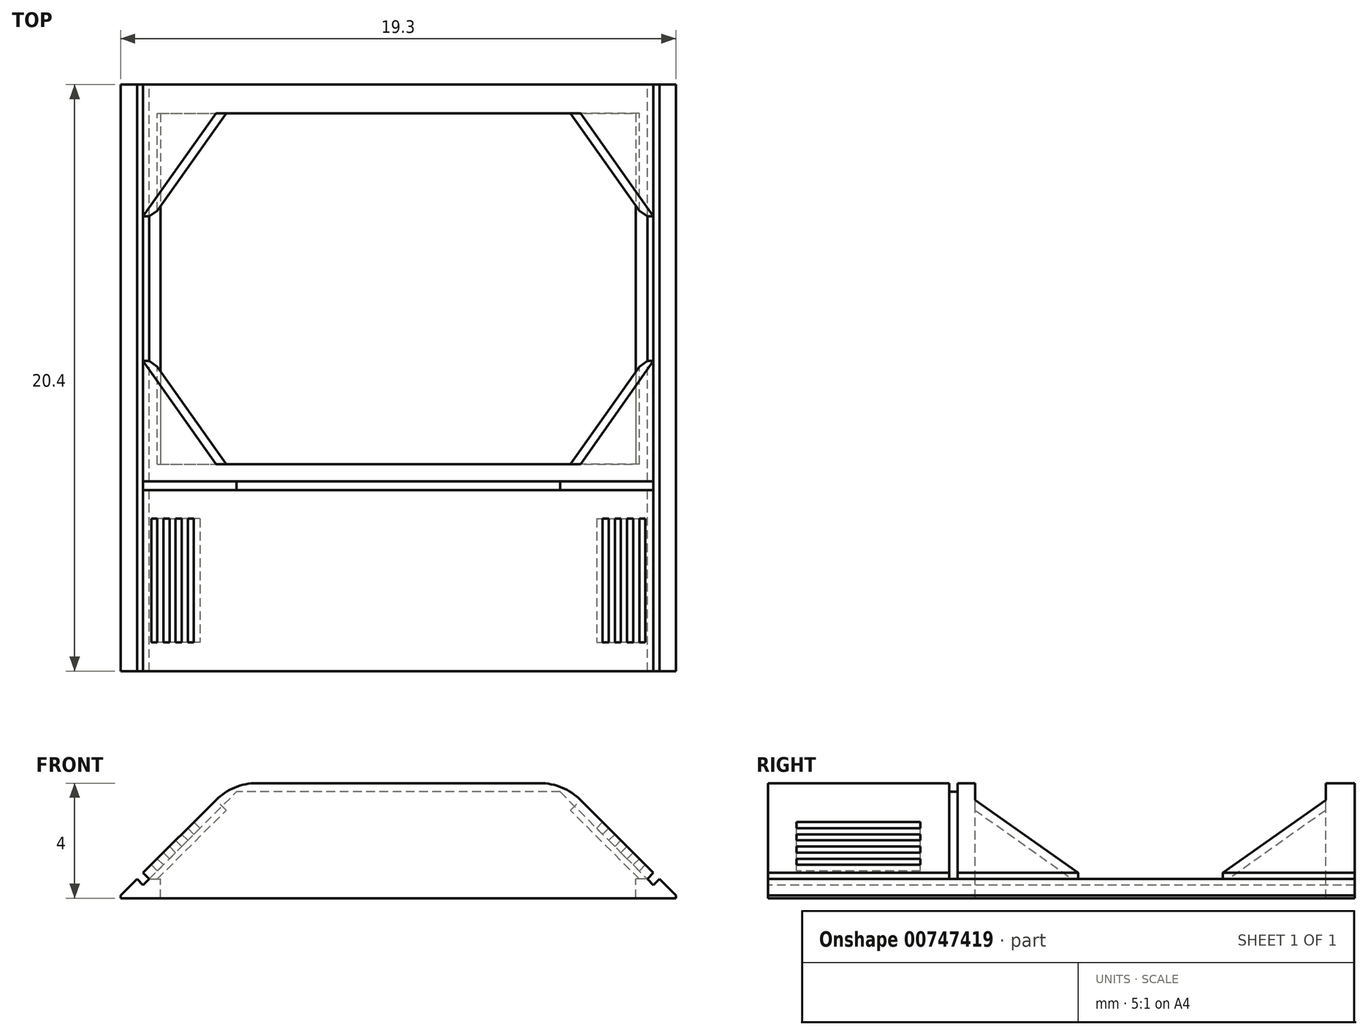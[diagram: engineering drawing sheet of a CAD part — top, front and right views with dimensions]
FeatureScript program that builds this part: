
annotation { "Feature Type Name" : "Feature", "Feature Type Description" : "" }
export const myFeature = defineFeature(function(context is Context, id is Id, definition is map)
    precondition{}
    {
        {
            var Q0;
            Q0=qCreatedBy(makeId("Front.planeOp"),FACE);
            var sketch = newSketch(context, id + "F0", { "sketchPlane" : qUnion([Q0])});
            skLineSegment(sketch, "E0", {"start": v(0, 0) * mm, "end": v(0, 3.9) * mm});
            skLineSegment(sketch, "E1", {"start": v(0, 3.9) * mm, "end": v(-5.75, 3.9) * mm});
            skLineSegment(sketch, "E2", {"start": v(-5.75, 3.9) * mm, "end": v(-9.65, 0) * mm});
            skLineSegment(sketch, "E3", {"start": v(-9.65, 0) * mm, "end": v(0, 0) * mm});
            skSolve(sketch);
        }
        {
            var Q0;
            Q0 = qSketchRegion(id + "F0", true);
            extrude(context, id + "F1", {"entities" : qUnion([Q0]), "depth" : 20.4 * mm, "offsetDistance" : 25 * mm});
        }
        {
            var Q0;
            Q0=makeQuery(id+"F1.opExtrude","SWEPT_FACE",FACE,{"disambiguationData":[OSD([sQuery(id+"F0.wireOp",EDGE,"E2")])]});
            var sketch = newSketch(context, id + "F2", { "sketchPlane" : qUnion([Q0])});
            skLineSegment(sketch, "E4", {"start": v(0, -5.72) * mm, "end": v(0, -6.02) * mm});
            skLineSegment(sketch, "E5", {"start": v(0, -6.02) * mm, "end": v(20.4, -6.02) * mm});
            skLineSegment(sketch, "E6", {"start": v(20.4, -5.72) * mm, "end": v(14.1, -5.72) * mm});
            skLineSegment(sketch, "E7", {"start": v(14.1, -5.72) * mm, "end": v(14.1, 0.2) * mm});
            skLineSegment(sketch, "E8", {"start": v(14.1, 0.2) * mm, "end": v(13.8, 0.2) * mm});
            skLineSegment(sketch, "E9", {"start": v(13.8, 0.2) * mm, "end": v(13.8, -5.72) * mm});
            skLineSegment(sketch, "E10", {"start": v(13.8, -5.72) * mm, "end": v(0, -5.72) * mm});
            skLineSegment(sketch, "E11", {"start": v(20.4, -5.72) * mm, "end": v(20.4, -6.02) * mm});
            skSolve(sketch);
        }
        {
            var Q0;
            Q0 = qSketchRegion(id + "F2", true);
            extrude(context, id + "F3", {"entities" : qUnion([Q0]), "operationType" : NewBodyOperationType.REMOVE, "oppositeDirection" : true, "depth" : 0.3 * mm, "offsetDistance" : 25 * mm});
        }
        {
            var Q0;
            Q0=makeQuery(id+"F1.opExtrude","SWEPT_FACE",FACE,{"disambiguationData":[OSD([sQuery(id+"F0.wireOp",EDGE,"E0")])]});
            var sketch = newSketch(context, id + "F4", { "sketchPlane" : qUnion([Q0])});
            skLineSegment(sketch, "E12", {"start": v(-13.2, 3.9) * mm, "end": v(-13.2, 0.57) * mm});
            skLineSegment(sketch, "E13", {"start": v(-13.2, 0.57) * mm, "end": v(-1, 0.57) * mm});
            skLineSegment(sketch, "E14", {"start": v(-1, 0.57) * mm, "end": v(-1, 3.9) * mm});
            skLineSegment(sketch, "E15", {"start": v(-1, 3.9) * mm, "end": v(-13.2, 3.9) * mm});
            skSolve(sketch);
        }
        {
            var Q0;
            Q0 = qSketchRegion(id + "F4", true);
            extrude(context, id + "F5", {"entities" : qUnion([Q0]), "operationType" : NewBodyOperationType.REMOVE, "endBound" : BoundingType.UP_TO_NEXT, "oppositeDirection" : true, "depth" : 25 * mm, "offsetDistance" : 25 * mm});
        }
        {
            var Q0;
            Q0=makeQuery(id+"F5.boolean.opBoolean","COPY",FACE,{"derivedFrom":makeQuery(id+"F5.opExtrude","SWEPT_FACE",FACE,{"disambiguationData":[OSD([sQuery(id+"F4.wireOp",EDGE,"E13")])]})});
            var sketch = newSketch(context, id + "F6", { "sketchPlane" : qUnion([Q0])});
            skLineSegment(sketch, "E16.bottom", {"start": v(0, -1) * mm, "end": v(-8.26, -1) * mm});
            skLineSegment(sketch, "E16.top", {"start": v(0, -13.2) * mm, "end": v(-8.26, -13.2) * mm});
            skLineSegment(sketch, "E16.left", {"start": v(0, -1) * mm, "end": v(0, -13.2) * mm});
            skLineSegment(sketch, "E16.right", {"start": v(-8.26, -1) * mm, "end": v(-8.26, -13.2) * mm});
            skSolve(sketch);
        }
        {
            var Q0;
            Q0 = qSketchRegion(id + "F6", true);
            extrude(context, id + "F7", {"entities" : qUnion([Q0]), "operationType" : NewBodyOperationType.REMOVE, "oppositeDirection" : true, "depth" : 25 * mm, "offsetDistance" : 25 * mm});
        }
        {
            var Q0;
            {var subQ0=sQuery(id+"F0.wireOp",EDGE,"E2");Q0=makeQuery(id+"F3.boolean.opBoolean","SPLIT",FACE,{"disambiguationData":[TD([makeQuery(id+"F3.opExtrude","SWEPT_FACE",FACE,{"disambiguationData":[OSD([sQuery(id+"F2.wireOp",EDGE,"E6")])]})])],"derivedFrom":makeQuery(id+"F1.opExtrude","SWEPT_FACE",FACE,{"disambiguationData":[OSD([subQ0])]})});}
            var sketch = newSketch(context, id + "F8", { "sketchPlane" : qUnion([Q0])});
            skLineSegment(sketch, "E17.bottom", {"start": v(15.1, -3.22) * mm, "end": v(19.4, -3.22) * mm});
            skLineSegment(sketch, "E17.top", {"start": v(15.1, -3.52) * mm, "end": v(19.4, -3.52) * mm});
            skLineSegment(sketch, "E17.left", {"start": v(15.1, -3.22) * mm, "end": v(15.1, -3.52) * mm});
            skLineSegment(sketch, "E17.right", {"start": v(19.4, -3.22) * mm, "end": v(19.4, -3.52) * mm});
            skLineSegment(sketch, "E18.bottom", {"start": v(15.1, -3.82) * mm, "end": v(19.4, -3.82) * mm});
            skLineSegment(sketch, "E18.top", {"start": v(15.1, -4.12) * mm, "end": v(19.4, -4.12) * mm});
            skLineSegment(sketch, "E18.left", {"start": v(15.1, -3.82) * mm, "end": v(15.1, -4.12) * mm});
            skLineSegment(sketch, "E18.right", {"start": v(19.4, -3.82) * mm, "end": v(19.4, -4.12) * mm});
            skLineSegment(sketch, "E19.bottom", {"start": v(15.1, -5.02) * mm, "end": v(19.4, -5.02) * mm});
            skLineSegment(sketch, "E19.top", {"start": v(15.1, -5.32) * mm, "end": v(19.4, -5.32) * mm});
            skLineSegment(sketch, "E19.left", {"start": v(15.1, -5.02) * mm, "end": v(15.1, -5.32) * mm});
            skLineSegment(sketch, "E19.right", {"start": v(19.4, -5.02) * mm, "end": v(19.4, -5.32) * mm});
            skLineSegment(sketch, "E20", {"start": v(19.4, -3.82) * mm, "end": v(19.4, -3.52) * mm, "construction": true});
            skLineSegment(sketch, "E21.bottom", {"start": v(15.1, -4.72) * mm, "end": v(19.4, -4.72) * mm});
            skLineSegment(sketch, "E21.top", {"start": v(15.1, -4.42) * mm, "end": v(19.4, -4.42) * mm});
            skLineSegment(sketch, "E21.left", {"start": v(15.1, -4.72) * mm, "end": v(15.1, -4.42) * mm});
            skLineSegment(sketch, "E21.right", {"start": v(19.4, -4.72) * mm, "end": v(19.4, -4.42) * mm});
            skLineSegment(sketch, "E22", {"start": v(19.4, -5.02) * mm, "end": v(19.4, -4.72) * mm, "construction": true});
            skLineSegment(sketch, "E23", {"start": v(19.4, -4.42) * mm, "end": v(19.4, -4.12) * mm, "construction": true});
            skSolve(sketch);
        }
        {
            var Q0;
            Q0 = qSketchRegion(id + "F8", true);
            extrude(context, id + "F9", {"entities" : qUnion([Q0]), "operationType" : NewBodyOperationType.REMOVE, "oppositeDirection" : true, "depth" : 0.3 * mm, "offsetDistance" : 25 * mm});
        }
        {
            var Q0;
            {var subQ0=sQuery(id+"F0.wireOp",EDGE,"E2");var subQ1=sQuery(id+"F0.wireOp",EDGE,"E1");Q0=makeQuery(id+"F3.boolean.opBoolean","SPLIT",EDGE,{"disambiguationData":[TD([makeQuery(id+"F3.opExtrude","SWEPT_FACE",FACE,{"disambiguationData":[OSD([sQuery(id+"F2.wireOp",EDGE,"f21vu9gR-xKNE-jHTs-my54-qgl62lx18LQn")])]})])],"derivedFrom":makeQuery(id+"F1.opExtrude","SWEPT_EDGE",EDGE,{"disambiguationData":[OSD([subQ1,subQ0])]})});}
            var Q1;
            Q1=makeQuery(id+"F9.boolean.opBoolean","INTERSECT",EDGE,{"derivedFrom":[makeQuery(id+"F3.boolean.opBoolean","COPY",FACE,{"derivedFrom":makeQuery(id+"F3.opExtrude","CAP_FACE",FACE,{"disambiguationData":[OSD([sQuery(id+"F2.wireOp",EDGE,"E4"),sQuery(id+"F2.wireOp",EDGE,"E5"),sQuery(id+"F2.wireOp",EDGE,"W1S3Mdm3-XKtb-n79g-vNsw-S0DXEWbo00DY"),sQuery(id+"F2.wireOp",EDGE,"qYD3X6LT-LOBn-4FV6-n4hA-iwyxqi3YV5cj"),sQuery(id+"F2.wireOp",EDGE,"E6"),sQuery(id+"F2.wireOp",EDGE,"E7"),sQuery(id+"F2.wireOp",EDGE,"E8"),sQuery(id+"F2.wireOp",EDGE,"E9"),sQuery(id+"F2.wireOp",EDGE,"E10"),sQuery(id+"F2.wireOp",EDGE,"NPIpTUiE-nrGw-dl87-8o0Y-yswYt9O5n7NW"),sQuery(id+"F2.wireOp",EDGE,"A6FpXCl3-eOSp-HMbo-aC3y-wrRHpwpuDLvK"),sQuery(id+"F2.wireOp",EDGE,"f21vu9gR-xKNE-jHTs-my54-qgl62lx18LQn"),sQuery(id+"F2.wireOp",EDGE,"PXoNwWFW-rPbD-wsng-xjVY-AKnaFY8J5v1U"),sQuery(id+"F2.wireOp",EDGE,"QdudRzUA-Mg1N-fK48-y1j2-ZxyqQCj9d9Z8")])],"isStart":false})}),makeQuery(id+"F9.opExtrude","CAP_FACE",FACE,{"disambiguationData":[OSD([sQuery(id+"F8.wireOp",EDGE,"rv0lEkuu-8LjM-F8fy-3w45-rrlrnGDjvpog.bottom"),sQuery(id+"F8.wireOp",EDGE,"rv0lEkuu-8LjM-F8fy-3w45-rrlrnGDjvpog.top"),sQuery(id+"F8.wireOp",EDGE,"rv0lEkuu-8LjM-F8fy-3w45-rrlrnGDjvpog.left"),sQuery(id+"F8.wireOp",EDGE,"rv0lEkuu-8LjM-F8fy-3w45-rrlrnGDjvpog.right")])],"isStart":false})]});
            var Q2;
            {var subQ0=sQuery(id+"F0.wireOp",EDGE,"E1");var subQ2=sQuery(id+"F0.wireOp",EDGE,"E2");var subQ4=makeQuery(id+"F3.opExtrude","SWEPT_FACE",FACE,{"disambiguationData":[OSD([sQuery(id+"F2.wireOp",EDGE,"NPIpTUiE-nrGw-dl87-8o0Y-yswYt9O5n7NW")])]});Q2=makeQuery(id+"F5.boolean.opBoolean","SPLIT",EDGE,{"disambiguationData":[TD([makeQuery(id+"F3.boolean.opBoolean","COPY",FACE,{"derivedFrom":subQ4})])],"derivedFrom":makeQuery(id+"F3.boolean.opBoolean","SPLIT",EDGE,{"disambiguationData":[TD([makeQuery(id+"F3.opExtrude","SWEPT_FACE",FACE,{"disambiguationData":[OSD([sQuery(id+"F2.wireOp",EDGE,"E9")])]})])],"derivedFrom":makeQuery(id+"F1.opExtrude","SWEPT_EDGE",EDGE,{"disambiguationData":[OSD([subQ0,subQ2])]})})});}
            var Q3;
            {var subQ0=sQuery(id+"F0.wireOp",EDGE,"E1");var subQ2=sQuery(id+"F0.wireOp",EDGE,"E2");var subQ4=makeQuery(id+"F3.opExtrude","SWEPT_FACE",FACE,{"disambiguationData":[OSD([sQuery(id+"F2.wireOp",EDGE,"E9")])]});Q3=makeQuery(id+"F5.boolean.opBoolean","SPLIT",EDGE,{"disambiguationData":[TD([makeQuery(id+"F3.boolean.opBoolean","COPY",FACE,{"derivedFrom":subQ4})])],"derivedFrom":makeQuery(id+"F3.boolean.opBoolean","SPLIT",EDGE,{"disambiguationData":[TD([subQ4])],"derivedFrom":makeQuery(id+"F1.opExtrude","SWEPT_EDGE",EDGE,{"disambiguationData":[OSD([subQ0,subQ2])]})})});}
            var Q4;
            Q4=makeQuery(id+"F9.boolean.opBoolean","INTERSECT",EDGE,{"derivedFrom":[makeQuery(id+"F3.boolean.opBoolean","COPY",FACE,{"derivedFrom":makeQuery(id+"F3.opExtrude","CAP_FACE",FACE,{"disambiguationData":[OSD([sQuery(id+"F2.wireOp",EDGE,"E4"),sQuery(id+"F2.wireOp",EDGE,"E5"),sQuery(id+"F2.wireOp",EDGE,"W1S3Mdm3-XKtb-n79g-vNsw-S0DXEWbo00DY"),sQuery(id+"F2.wireOp",EDGE,"qYD3X6LT-LOBn-4FV6-n4hA-iwyxqi3YV5cj"),sQuery(id+"F2.wireOp",EDGE,"E6"),sQuery(id+"F2.wireOp",EDGE,"E7"),sQuery(id+"F2.wireOp",EDGE,"E8"),sQuery(id+"F2.wireOp",EDGE,"E9"),sQuery(id+"F2.wireOp",EDGE,"E10"),sQuery(id+"F2.wireOp",EDGE,"NPIpTUiE-nrGw-dl87-8o0Y-yswYt9O5n7NW"),sQuery(id+"F2.wireOp",EDGE,"A6FpXCl3-eOSp-HMbo-aC3y-wrRHpwpuDLvK"),sQuery(id+"F2.wireOp",EDGE,"f21vu9gR-xKNE-jHTs-my54-qgl62lx18LQn"),sQuery(id+"F2.wireOp",EDGE,"PXoNwWFW-rPbD-wsng-xjVY-AKnaFY8J5v1U"),sQuery(id+"F2.wireOp",EDGE,"QdudRzUA-Mg1N-fK48-y1j2-ZxyqQCj9d9Z8")])],"isStart":false})}),makeQuery(id+"F9.opExtrude","CAP_FACE",FACE,{"disambiguationData":[OSD([sQuery(id+"F8.wireOp",EDGE,"9kW2MHKQ-ooD5-zoGo-1hlY-vFjgnSLi35nN.bottom"),sQuery(id+"F8.wireOp",EDGE,"9kW2MHKQ-ooD5-zoGo-1hlY-vFjgnSLi35nN.top"),sQuery(id+"F8.wireOp",EDGE,"9kW2MHKQ-ooD5-zoGo-1hlY-vFjgnSLi35nN.left"),sQuery(id+"F8.wireOp",EDGE,"9kW2MHKQ-ooD5-zoGo-1hlY-vFjgnSLi35nN.right")])],"isStart":false})]});
            var Q5;
            {var subQ0=sQuery(id+"F0.wireOp",EDGE,"E1");var subQ1=sQuery(id+"F0.wireOp",EDGE,"E2");Q5=makeQuery(id+"F3.boolean.opBoolean","SPLIT",EDGE,{"disambiguationData":[TD([makeQuery(id+"F3.opExtrude","SWEPT_FACE",FACE,{"disambiguationData":[OSD([sQuery(id+"F2.wireOp",EDGE,"qYD3X6LT-LOBn-4FV6-n4hA-iwyxqi3YV5cj")])]})])],"derivedFrom":makeQuery(id+"F1.opExtrude","SWEPT_EDGE",EDGE,{"disambiguationData":[OSD([subQ0,subQ1])]})});}
            var Q6;
            Q6=makeQuery(id+"F9.boolean.opBoolean","INTERSECT",EDGE,{"derivedFrom":[makeQuery(id+"F3.boolean.opBoolean","COPY",FACE,{"derivedFrom":makeQuery(id+"F3.opExtrude","CAP_FACE",FACE,{"disambiguationData":[OSD([sQuery(id+"F2.wireOp",EDGE,"E4"),sQuery(id+"F2.wireOp",EDGE,"E5"),sQuery(id+"F2.wireOp",EDGE,"W1S3Mdm3-XKtb-n79g-vNsw-S0DXEWbo00DY"),sQuery(id+"F2.wireOp",EDGE,"qYD3X6LT-LOBn-4FV6-n4hA-iwyxqi3YV5cj"),sQuery(id+"F2.wireOp",EDGE,"E6"),sQuery(id+"F2.wireOp",EDGE,"E7"),sQuery(id+"F2.wireOp",EDGE,"E8"),sQuery(id+"F2.wireOp",EDGE,"E9"),sQuery(id+"F2.wireOp",EDGE,"E10"),sQuery(id+"F2.wireOp",EDGE,"NPIpTUiE-nrGw-dl87-8o0Y-yswYt9O5n7NW"),sQuery(id+"F2.wireOp",EDGE,"A6FpXCl3-eOSp-HMbo-aC3y-wrRHpwpuDLvK"),sQuery(id+"F2.wireOp",EDGE,"f21vu9gR-xKNE-jHTs-my54-qgl62lx18LQn"),sQuery(id+"F2.wireOp",EDGE,"PXoNwWFW-rPbD-wsng-xjVY-AKnaFY8J5v1U"),sQuery(id+"F2.wireOp",EDGE,"QdudRzUA-Mg1N-fK48-y1j2-ZxyqQCj9d9Z8")])],"isStart":false})}),makeQuery(id+"F9.opExtrude","CAP_FACE",FACE,{"disambiguationData":[OSD([sQuery(id+"F8.wireOp",EDGE,"ZSyIJnYn-PckX-nyar-pei3-2CxvSKr0QWU7.bottom"),sQuery(id+"F8.wireOp",EDGE,"ZSyIJnYn-PckX-nyar-pei3-2CxvSKr0QWU7.top"),sQuery(id+"F8.wireOp",EDGE,"ZSyIJnYn-PckX-nyar-pei3-2CxvSKr0QWU7.left"),sQuery(id+"F8.wireOp",EDGE,"ZSyIJnYn-PckX-nyar-pei3-2CxvSKr0QWU7.right")])],"isStart":false})]});
            var Q7;
            {var subQ0=sQuery(id+"F0.wireOp",EDGE,"E2");var subQ1=sQuery(id+"F0.wireOp",EDGE,"E1");Q7=makeQuery(id+"F3.boolean.opBoolean","SPLIT",EDGE,{"disambiguationData":[TD([makeQuery(id+"F3.opExtrude","SWEPT_FACE",FACE,{"disambiguationData":[OSD([sQuery(id+"F2.wireOp",EDGE,"QdudRzUA-Mg1N-fK48-y1j2-ZxyqQCj9d9Z8")])]})])],"derivedFrom":makeQuery(id+"F1.opExtrude","SWEPT_EDGE",EDGE,{"disambiguationData":[OSD([subQ1,subQ0])]})});}
            var Q8;
            {var subQ0=sQuery(id+"F0.wireOp",EDGE,"E2");var subQ1=sQuery(id+"F0.wireOp",EDGE,"E1");Q8=makeQuery(id+"F5.boolean.opBoolean","SPLIT",EDGE,{"disambiguationData":[TD([makeQuery(id+"F5.opExtrude","SWEPT_FACE",FACE,{"disambiguationData":[OSD([sQuery(id+"F4.wireOp",EDGE,"E14")])]})])],"derivedFrom":makeQuery(id+"F3.boolean.opBoolean","SPLIT",EDGE,{"disambiguationData":[TD([makeQuery(id+"F3.opExtrude","SWEPT_FACE",FACE,{"disambiguationData":[OSD([sQuery(id+"F2.wireOp",EDGE,"E9")])]})])],"derivedFrom":makeQuery(id+"F1.opExtrude","SWEPT_EDGE",EDGE,{"disambiguationData":[OSD([subQ1,subQ0])]})})});}
            fillet(context, id + "F10", {"entities" : qUnion([Q0, Q1, Q2, Q3, Q4, Q5, Q6, Q7, Q8]), "radius" : 2 * mm, "tangentPropagation" : true, "allowEdgeOverflow" : false});
        }
        {
            var Q0;
            {var subQ1=makeQuery(id+"F3.opExtrude","SWEPT_FACE",FACE,{"disambiguationData":[OSD([sQuery(id+"F2.wireOp",EDGE,"E9")])]});Q0=makeQuery(id+"F5.boolean.opBoolean","SPLIT",FACE,{"disambiguationData":[TD([makeQuery(id+"F3.boolean.opBoolean","COPY",FACE,{"derivedFrom":subQ1})])],"derivedFrom":makeQuery(id+"F3.boolean.opBoolean","SPLIT",FACE,{"disambiguationData":[TD([subQ1])],"derivedFrom":makeQuery(id+"F1.opExtrude","SWEPT_FACE",FACE,{"disambiguationData":[OSD([sQuery(id+"F0.wireOp",EDGE,"E2")])]})})});}
            var sketch = newSketch(context, id + "F11", { "sketchPlane" : qUnion([Q0])});
            skLineSegment(sketch, "E24", {"start": v(13.2, -2.14) * mm, "end": v(9.61, -5.72) * mm});
            skLineSegment(sketch, "E25", {"start": v(9.61, -5.72) * mm, "end": v(13.2, -5.72) * mm});
            skLineSegment(sketch, "E26", {"start": v(1, -5.72) * mm, "end": v(1, -2.14) * mm});
            skLineSegment(sketch, "E27", {"start": v(1, -2.14) * mm, "end": v(4.59, -5.72) * mm});
            skLineSegment(sketch, "E28", {"start": v(4.59, -5.72) * mm, "end": v(1, -5.72) * mm});
            skSolve(sketch);
        }
        {
            var Q0;
            Q0 = qSketchRegion(id + "F11", true);
            var Q1;
            Q1=makeQuery(id+"F11.imprint","IMPRINT",FACE,{"disambiguationData":[TD([[makeQuery(id+"F11.imprint","IMPRINT",EDGE,{"derivedFrom":sQuery(id+"F11.wireOp",EDGE,"E24")}),1.0]])]});
            extrude(context, id + "F12", {"entities" : qUnion([Q0, Q1]), "operationType" : NewBodyOperationType.ADD, "oppositeDirection" : true, "depth" : 0.5 * mm, "offsetDistance" : 25 * mm});
        }
        {
            var Q0;
            {var subQ1=sQuery(id+"F2.wireOp",EDGE,"E7");var subQ3=sQuery(id+"F0.wireOp",EDGE,"E1");Q0=makeQuery(id+"F5.boolean.opBoolean","SPLIT",FACE,{"disambiguationData":[TD([makeQuery(id+"F3.boolean.opBoolean","COPY",FACE,{"derivedFrom":makeQuery(id+"F3.opExtrude","SWEPT_FACE",FACE,{"disambiguationData":[OSD([subQ1])]})})])],"derivedFrom":makeQuery(id+"F1.opExtrude","SWEPT_FACE",FACE,{"disambiguationData":[OSD([subQ3])]})});}
            var sketch = newSketch(context, id + "F13", { "sketchPlane" : qUnion([Q0])});
            skLineSegment(sketch, "E29.bottom", {"start": v(0, -14.1) * mm, "end": v(-8.87, -14.1) * mm});
            skLineSegment(sketch, "E29.top", {"start": v(0, -13.8) * mm, "end": v(-8.87, -13.8) * mm});
            skLineSegment(sketch, "E29.left", {"start": v(0, -14.1) * mm, "end": v(0, -13.8) * mm});
            skLineSegment(sketch, "E29.right", {"start": v(-8.87, -14.1) * mm, "end": v(-8.87, -13.8) * mm});
            skSolve(sketch);
        }
        {
            var Q0;
            Q0 = qSketchRegion(id + "F13", true);
            extrude(context, id + "F14", {"entities" : qUnion([Q0]), "operationType" : NewBodyOperationType.REMOVE, "oppositeDirection" : true, "depth" : 0.3 * mm, "offsetDistance" : 25 * mm});
        }
        {
            var Q0;
            Q0=makeQuery(id+"F1.opExtrude","SWEPT_BODY",BODY,{"disambiguationData":[OSD([sQuery(id+"F0.wireOp",EDGE,"E0"),sQuery(id+"F0.wireOp",EDGE,"E1"),sQuery(id+"F0.wireOp",EDGE,"E2"),sQuery(id+"F0.wireOp",EDGE,"E3")])]});
            var Q1;
            {var subQ2=sQuery(id+"F0.wireOp",EDGE,"E0");Q1=makeQuery(id+"F7.boolean.opBoolean","SPLIT",FACE,{"disambiguationData":[TD([makeQuery(id+"F5.boolean.opBoolean","COPY",FACE,{"derivedFrom":makeQuery(id+"F5.opExtrude","SWEPT_FACE",FACE,{"disambiguationData":[OSD([sQuery(id+"F4.wireOp",EDGE,"E12")])]})})])],"derivedFrom":makeQuery(id+"F1.opExtrude","SWEPT_FACE",FACE,{"disambiguationData":[OSD([subQ2])]})});}
            mirror(context, id + "F15", {"operationType" : NewBodyOperationType.ADD, "entities" : qUnion([Q0]), "mirrorPlane" : qUnion([Q1])});
        }
        {
            var Q0;
            {var subQ0=makeQuery(id+"F1.opExtrude","SWEPT_FACE",FACE,{"disambiguationData":[OSD([sQuery(id+"F0.wireOp",EDGE,"E3")])]});Q0=makeQuery(id+"F15.boolean.opBoolean","MERGE",FACE,{"derivedFrom":[subQ0,makeQuery(id+"F15.opPattern","COPY",FACE,{"derivedFrom":subQ0,"instanceName":"1"})]});}
            extrude(context, id + "F16", {"entities" : qUnion([Q0]), "operationType" : NewBodyOperationType.ADD, "depth" : 0.1 * mm, "offsetDistance" : 25 * mm});
        }
    });
